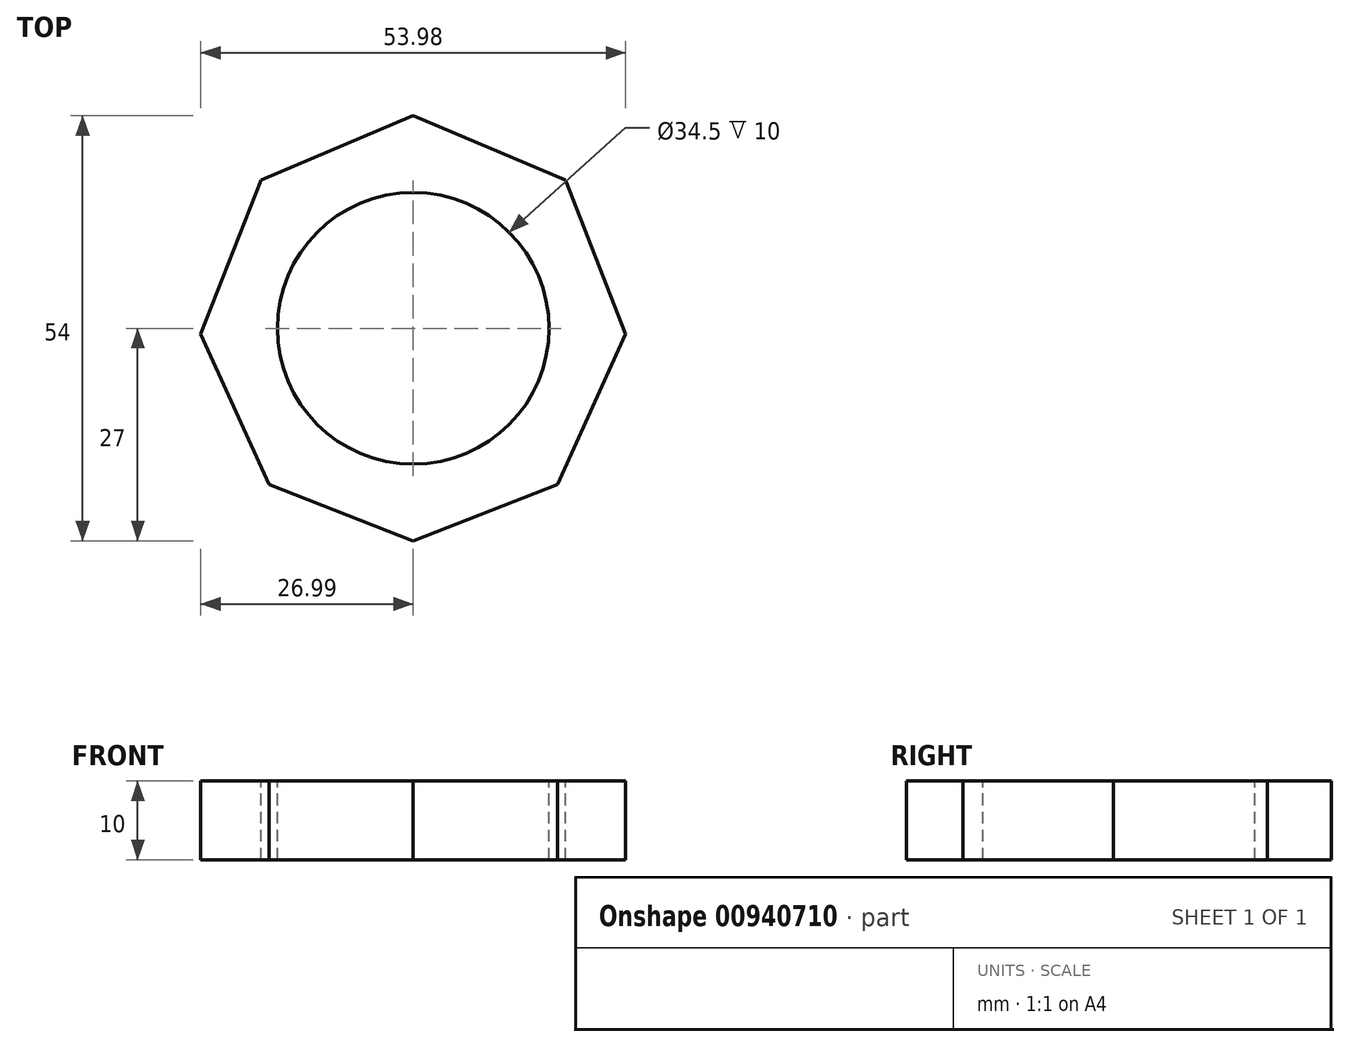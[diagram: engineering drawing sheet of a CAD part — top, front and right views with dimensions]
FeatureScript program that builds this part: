
annotation { "Feature Type Name" : "Feature", "Feature Type Description" : "" }
export const myFeature = defineFeature(function(context is Context, id is Id, definition is map)
    precondition{}
    {
        {
            var Q0;
            Q0=qCreatedBy(makeId("Top.planeOp"),FACE);
            var sketch = newSketch(context, id + "F0", { "sketchPlane" : qUnion([Q0])});
            skCircle(sketch, "E0", {"center": v(0, 0) * mm, "radius": 27 * mm});
            skSolve(sketch);
        }
        {
            var Q0;
            Q0 = qSketchRegion(id + "F0", true);
            extrude(context, id + "F1", {"entities" : qUnion([Q0]), "depth" : 10 * mm, "offsetDistance" : 25 * mm});
        }
        {
            var Q0;
            Q0=makeQuery(id+"F1.opExtrude","CAP_FACE",FACE,{"disambiguationData":[OSD([sQuery(id+"F0.wireOp",EDGE,"E0")])],"isStart":false});
            var sketch = newSketch(context, id + "F2", { "sketchPlane" : qUnion([Q0])});
            skCircle(sketch, "E1", {"center": v(0, 0) * mm, "radius": 17.25 * mm});
            skSolve(sketch);
        }
        {
            var Q0;
            Q0 = qSketchRegion(id + "F2", true);
            extrude(context, id + "F3", {"entities" : qUnion([Q0]), "operationType" : NewBodyOperationType.REMOVE, "oppositeDirection" : true, "depth" : 25 * mm, "offsetDistance" : 25 * mm});
        }
        {
            var Q0;
            Q0=makeQuery(id+"F1.opExtrude","CAP_FACE",FACE,{"disambiguationData":[OSD([sQuery(id+"F0.wireOp",EDGE,"E0")])],"isStart":false});
            var sketch = newSketch(context, id + "F4", { "sketchPlane" : qUnion([Q0])});
            skLineSegment(sketch, "E2", {"start": v(0, 27) * mm, "end": v(-19.35, 18.83) * mm});
            skLineSegment(sketch, "E3", {"start": v(-19.35, 18.83) * mm, "end": v(-27, -0.73) * mm});
            skLineSegment(sketch, "E4", {"start": v(-27, -0.73) * mm, "end": v(-18.3, -19.85) * mm});
            skLineSegment(sketch, "E5", {"start": v(-18.3, -19.85) * mm, "end": v(0, -27) * mm});
            skLineSegment(sketch, "E6", {"start": v(0, 27) * mm, "end": v(0, -27) * mm, "construction": true});
            skLineSegment(sketch, "E7.MirrorCS", {"start": v(0, 27) * mm, "end": v(19.35, 18.83) * mm});
            skLineSegment(sketch, "E8.MirrorCS", {"start": v(19.35, 18.83) * mm, "end": v(27, -0.73) * mm});
            skLineSegment(sketch, "E9.MirrorCS", {"start": v(27, -0.73) * mm, "end": v(18.3, -19.85) * mm});
            skLineSegment(sketch, "E10.MirrorCS", {"start": v(18.3, -19.85) * mm, "end": v(0, -27) * mm});
            skSolve(sketch);
        }
        {
            var Q0;
            {var subQ0=sQuery(id+"F4.wireOp",EDGE,"E3");Q0=makeQuery(id+"F4.imprint","IMPRINT",FACE,{"disambiguationData":[TD([[makeQuery(id+"F4.imprint","IMPRINT",EDGE,{"derivedFrom":subQ0}),-1.0]])]});}
            var Q1;
            {var subQ0=sQuery(id+"F4.wireOp",EDGE,"E2");Q1=makeQuery(id+"F4.imprint","IMPRINT",FACE,{"disambiguationData":[TD([[makeQuery(id+"F4.imprint","IMPRINT",EDGE,{"derivedFrom":subQ0}),-1.0]])]});}
            var Q2;
            {var subQ0=sQuery(id+"F4.wireOp",EDGE,"E7.MirrorCS");Q2=makeQuery(id+"F4.imprint","IMPRINT",FACE,{"disambiguationData":[TD([[makeQuery(id+"F4.imprint","IMPRINT",EDGE,{"derivedFrom":subQ0}),1.0]])]});}
            var Q3;
            {var subQ0=sQuery(id+"F4.wireOp",EDGE,"E8.MirrorCS");Q3=makeQuery(id+"F4.imprint","IMPRINT",FACE,{"disambiguationData":[TD([[makeQuery(id+"F4.imprint","IMPRINT",EDGE,{"derivedFrom":subQ0}),1.0]])]});}
            var Q4;
            {var subQ0=sQuery(id+"F4.wireOp",EDGE,"E9.MirrorCS");Q4=makeQuery(id+"F4.imprint","IMPRINT",FACE,{"disambiguationData":[TD([[makeQuery(id+"F4.imprint","IMPRINT",EDGE,{"derivedFrom":subQ0}),1.0]])]});}
            var Q5;
            {var subQ0=sQuery(id+"F4.wireOp",EDGE,"E10.MirrorCS");Q5=makeQuery(id+"F4.imprint","IMPRINT",FACE,{"disambiguationData":[TD([[makeQuery(id+"F4.imprint","IMPRINT",EDGE,{"derivedFrom":subQ0}),1.0]])]});}
            var Q6;
            {var subQ0=sQuery(id+"F4.wireOp",EDGE,"E5");Q6=makeQuery(id+"F4.imprint","IMPRINT",FACE,{"disambiguationData":[TD([[makeQuery(id+"F4.imprint","IMPRINT",EDGE,{"derivedFrom":subQ0}),-1.0]])]});}
            var Q7;
            {var subQ0=sQuery(id+"F4.wireOp",EDGE,"E4");Q7=makeQuery(id+"F4.imprint","IMPRINT",FACE,{"disambiguationData":[TD([[makeQuery(id+"F4.imprint","IMPRINT",EDGE,{"derivedFrom":subQ0}),-1.0]])]});}
            extrude(context, id + "F5", {"entities" : qUnion([Q0, Q1, Q2, Q3, Q4, Q5, Q6, Q7]), "operationType" : NewBodyOperationType.REMOVE, "oppositeDirection" : true, "depth" : 25 * mm, "offsetDistance" : 25 * mm});
        }
    });
